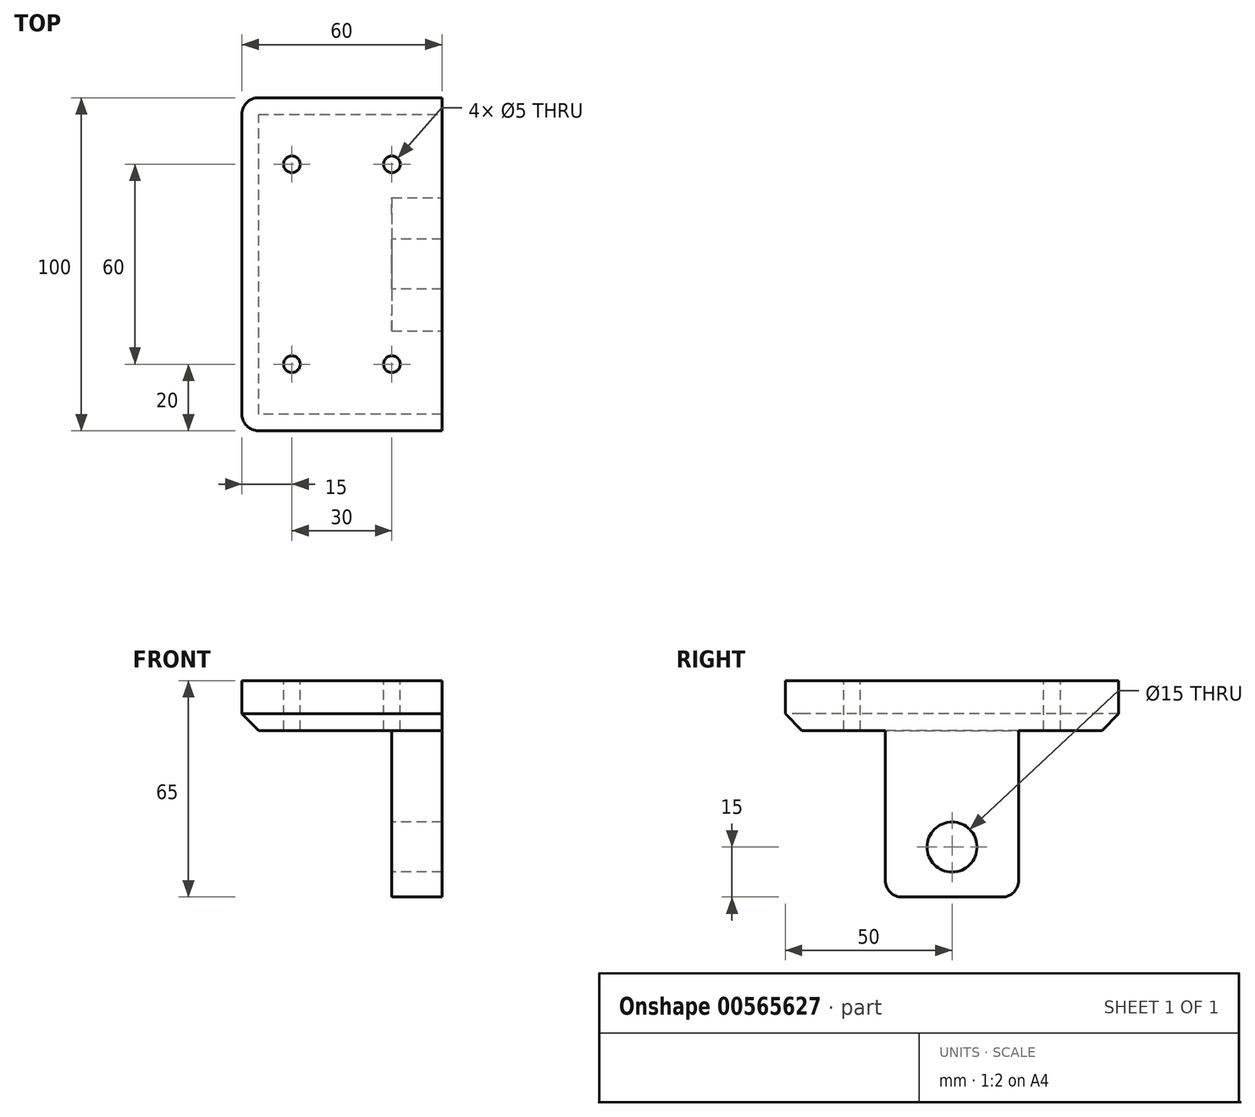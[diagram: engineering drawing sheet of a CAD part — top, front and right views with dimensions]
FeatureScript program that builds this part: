
annotation { "Feature Type Name" : "Feature", "Feature Type Description" : "" }
export const myFeature = defineFeature(function(context is Context, id is Id, definition is map)
    precondition{}
    {
        {
            var Q0;
            Q0=qCreatedBy(makeId("Top.planeOp"),FACE);
            var sketch = newSketch(context, id + "F0", { "sketchPlane" : qUnion([Q0])});
            skLineSegment(sketch, "E0.bottom", {"start": v(-25, 50) * mm, "end": v(30, 50) * mm});
            skLineSegment(sketch, "E0.top", {"start": v(-25, -50) * mm, "end": v(30, -50) * mm});
            skLineSegment(sketch, "E0.left", {"start": v(-30, 45) * mm, "end": v(-30, -45) * mm});
            skLineSegment(sketch, "E0.right", {"start": v(30, 50) * mm, "end": v(30, -50) * mm});
            skPoint(sketch, "E0.middle", {"position": v(0, 0) * mm});
            skPoint(sketch, "E1.visualSharp", {"position": v(-30, 50) * mm});
            skArc(sketch, "E1.filletArc", {"start": v(-25, 50) * mm, "mid": v(-28.54, 48.54) * mm, "end": v(-30, 45) * mm});
            skPoint(sketch, "E2.visualSharp", {"position": v(-30, -50) * mm});
            skArc(sketch, "E2.filletArc", {"start": v(-30, -45) * mm, "mid": v(-28.54, -48.54) * mm, "end": v(-25, -50) * mm});
            skSolve(sketch);
        }
        {
            var Q0;
            Q0=makeQuery(id+"F0.imprint","IMPRINT",FACE,{"disambiguationData":[TD([[makeQuery(id+"F0.imprint","IMPRINT",EDGE,{"derivedFrom":sQuery(id+"F0.wireOp",EDGE,"E0.bottom")}),-1.0]])]});
            extrude(context, id + "F1", {"entities" : qUnion([Q0]), "depth" : 15 * mm, "offsetDistance" : 25 * mm});
        }
        {
            var Q0;
            Q0=makeQuery(id+"F1.opExtrude","SWEPT_FACE",FACE,{"disambiguationData":[OSD([sQuery(id+"F0.wireOp",EDGE,"E0.right")])]});
            var sketch = newSketch(context, id + "F2", { "sketchPlane" : qUnion([Q0])});
            skLineSegment(sketch, "E3.bottom", {"start": v(20, 0) * mm, "end": v(-20, 0) * mm});
            skLineSegment(sketch, "E3.top", {"start": v(20, -50) * mm, "end": v(-20, -50) * mm});
            skLineSegment(sketch, "E3.left", {"start": v(20, 0) * mm, "end": v(20, -50) * mm});
            skLineSegment(sketch, "E3.right", {"start": v(-20, 0) * mm, "end": v(-20, -50) * mm});
            skSolve(sketch);
        }
        {
            var Q0;
            Q0 = qSketchRegion(id + "F2", true);
            extrude(context, id + "F3", {"entities" : qUnion([Q0]), "operationType" : NewBodyOperationType.ADD, "oppositeDirection" : true, "depth" : 15 * mm, "offsetDistance" : 25 * mm});
        }
        {
            var Q0;
            Q0=makeQuery(id+"F3.opExtrude","SWEPT_EDGE",EDGE,{"disambiguationData":[OSD([sQuery(id+"F0.wireOp",EDGE,"E0.right"),sQuery(id+"F2.wireOp",EDGE,"E3.bottom"),sQuery(id+"F2.wireOp",EDGE,"E3.left")])]});
            var Q1;
            Q1=makeQuery(id+"F3.opExtrude","CAP_EDGE",EDGE,{"disambiguationData":[OSD([sQuery(id+"F2.wireOp",EDGE,"E3.bottom")])],"isStart":false});
            var Q2;
            Q2=makeQuery(id+"F3.opExtrude","SWEPT_EDGE",EDGE,{"disambiguationData":[OSD([sQuery(id+"F2.wireOp",EDGE,"E3.top"),sQuery(id+"F2.wireOp",EDGE,"E3.left")])]});
            var Q3;
            Q3=makeQuery(id+"F3.opExtrude","SWEPT_EDGE",EDGE,{"disambiguationData":[OSD([sQuery(id+"F2.wireOp",EDGE,"E3.top"),sQuery(id+"F2.wireOp",EDGE,"E3.right")])]});
            var Q4;
            Q4=makeQuery(id+"F3.opExtrude","SWEPT_EDGE",EDGE,{"disambiguationData":[OSD([sQuery(id+"F0.wireOp",EDGE,"E0.right"),sQuery(id+"F2.wireOp",EDGE,"E3.bottom"),sQuery(id+"F2.wireOp",EDGE,"E3.right")])]});
            fillet(context, id + "F4", {"entities" : qUnion([Q0, Q1, Q2, Q3, Q4]), "radius" : 5 * mm, "tangentPropagation" : true, "allowEdgeOverflow" : false});
        }
        {
            var Q0;
            Q0=makeQuery(id+"F1.opExtrude","CAP_EDGE",EDGE,{"disambiguationData":[OSD([sQuery(id+"F0.wireOp",EDGE,"E0.bottom")])],"isStart":true});
            chamfer(context, id + "F5", {"entities" : qUnion([Q0]), "width" : 5 * mm, "tangentPropagation" : true});
        }
        {
            var Q0;
            Q0=makeQuery(id+"F3.opExtrude","CAP_FACE",FACE,{"disambiguationData":[OSD([sQuery(id+"F2.wireOp",EDGE,"E3.bottom"),sQuery(id+"F2.wireOp",EDGE,"E3.top"),sQuery(id+"F2.wireOp",EDGE,"E3.left"),sQuery(id+"F2.wireOp",EDGE,"E3.right")])],"isStart":false});
            var sketch = newSketch(context, id + "F6", { "sketchPlane" : qUnion([Q0])});
            skLineSegment(sketch, "E4", {"start": v(0, -47.14) * mm, "end": v(0, -9.12) * mm, "construction": true});
            skPoint(sketch, "E4.startSnap0", {"position": v(0, -5) * mm});
            skCircle(sketch, "E5", {"center": v(0, -35) * mm, "radius": 7.5 * mm});
            skSolve(sketch);
        }
        {
            var Q0;
            Q0=makeQuery(id+"F6.imprint","IMPRINT",FACE,{"disambiguationData":[TD([[makeQuery(id+"F6.imprint","IMPRINT",EDGE,{"derivedFrom":sQuery(id+"F6.wireOp",EDGE,"E5")}),1.0]])]});
            extrude(context, id + "F7", {"entities" : qUnion([Q0]), "operationType" : NewBodyOperationType.REMOVE, "oppositeDirection" : true, "depth" : 25 * mm, "offsetDistance" : 25 * mm});
        }
        {
            var Q0;
            Q0=makeQuery(id+"F1.opExtrude","CAP_FACE",FACE,{"disambiguationData":[OSD([sQuery(id+"F0.wireOp",EDGE,"E0.bottom"),sQuery(id+"F0.wireOp",EDGE,"E0.top"),sQuery(id+"F0.wireOp",EDGE,"E0.left"),sQuery(id+"F0.wireOp",EDGE,"E0.right"),sQuery(id+"F0.wireOp",EDGE,"E1.filletArc"),sQuery(id+"F0.wireOp",EDGE,"E2.filletArc")])],"isStart":false});
            var sketch = newSketch(context, id + "F8", { "sketchPlane" : qUnion([Q0])});
            skCircle(sketch, "E6", {"center": v(-15, 30) * mm, "radius": 2.5 * mm});
            skCircle(sketch, "E7.0.1.0", {"center": v(-15, -30) * mm, "radius": 2.5 * mm});
            skCircle(sketch, "E7.1.0.0", {"center": v(15, 30) * mm, "radius": 2.5 * mm});
            skCircle(sketch, "E7.1.1.0", {"center": v(15, -30) * mm, "radius": 2.5 * mm});
            skLineSegment(sketch, "E7.direction1", {"start": v(-15, 30) * mm, "end": v(15, 30) * mm, "construction": true});
            skLineSegment(sketch, "E7.direction2", {"start": v(-15, 30) * mm, "end": v(-15, -30) * mm, "construction": true});
            skSolve(sketch);
        }
        {
            var Q0;
            Q0=makeQuery(id+"F8.imprint","IMPRINT",FACE,{"disambiguationData":[TD([[makeQuery(id+"F8.imprint","IMPRINT",EDGE,{"derivedFrom":sQuery(id+"F8.wireOp",EDGE,"E7.0.1.0")}),1.0]])]});
            var Q1;
            Q1=makeQuery(id+"F8.imprint","IMPRINT",FACE,{"disambiguationData":[TD([[makeQuery(id+"F8.imprint","IMPRINT",EDGE,{"derivedFrom":sQuery(id+"F8.wireOp",EDGE,"E7.1.1.0")}),1.0]])]});
            var Q2;
            Q2=makeQuery(id+"F8.imprint","IMPRINT",FACE,{"disambiguationData":[TD([[makeQuery(id+"F8.imprint","IMPRINT",EDGE,{"derivedFrom":sQuery(id+"F8.wireOp",EDGE,"E7.1.0.0")}),1.0]])]});
            var Q3;
            Q3=makeQuery(id+"F8.imprint","IMPRINT",FACE,{"disambiguationData":[TD([[makeQuery(id+"F8.imprint","IMPRINT",EDGE,{"derivedFrom":sQuery(id+"F8.wireOp",EDGE,"E6")}),1.0]])]});
            extrude(context, id + "F9", {"entities" : qUnion([Q0, Q1, Q2, Q3]), "operationType" : NewBodyOperationType.REMOVE, "oppositeDirection" : true, "depth" : 25 * mm, "offsetDistance" : 25 * mm});
        }
    });
